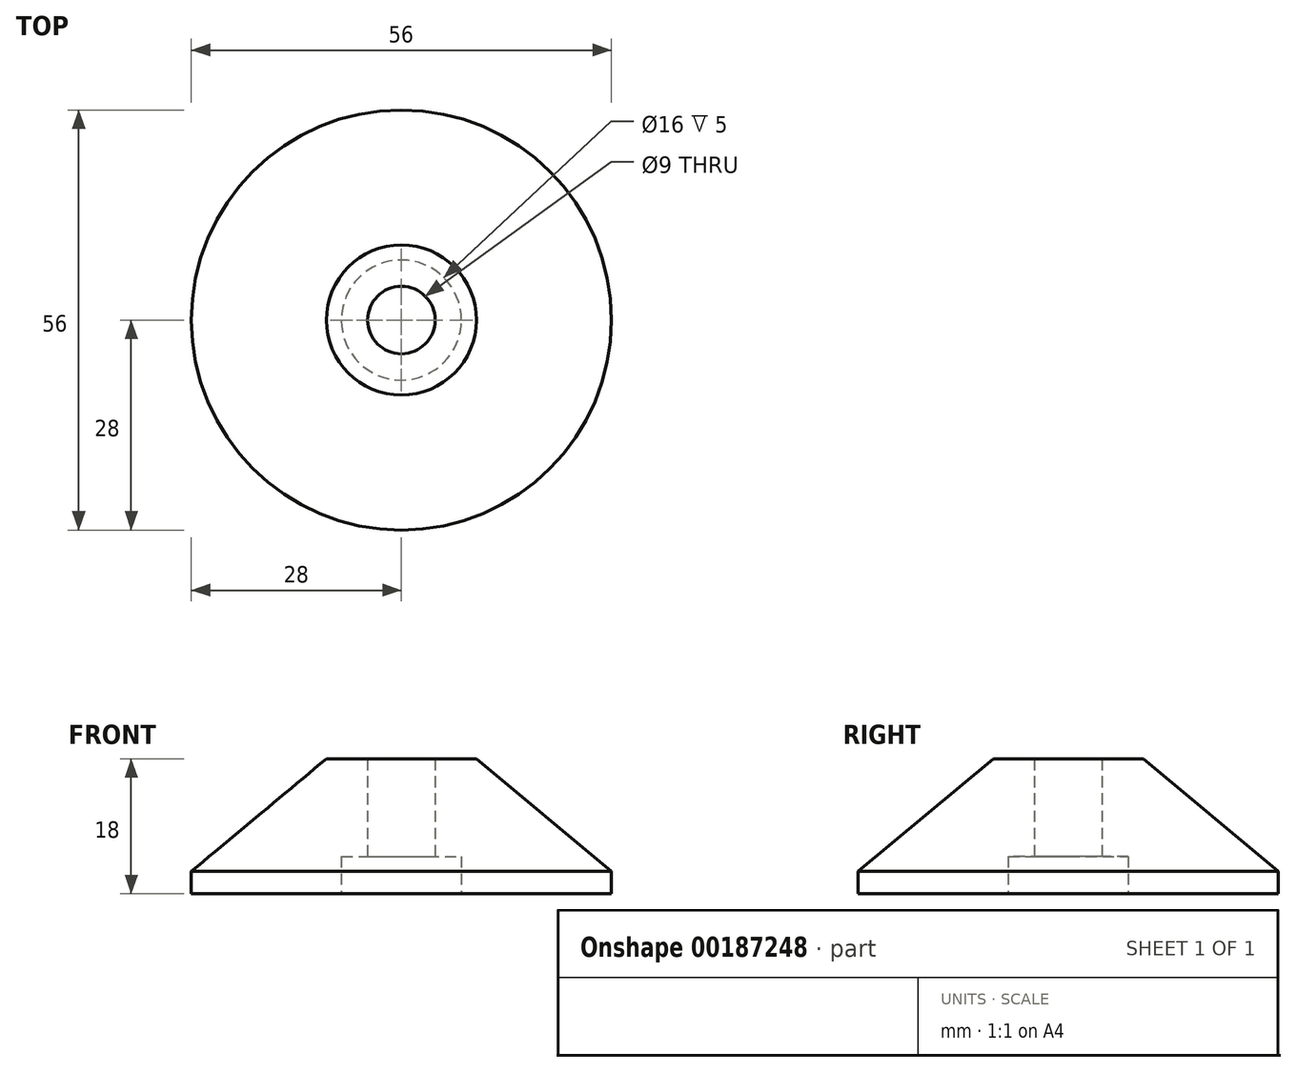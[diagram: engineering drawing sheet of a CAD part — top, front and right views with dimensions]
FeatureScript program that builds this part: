
annotation { "Feature Type Name" : "Feature", "Feature Type Description" : "" }
export const myFeature = defineFeature(function(context is Context, id is Id, definition is map)
    precondition{}
    {
        {
            var Q0;
            Q0=qCreatedBy(makeId("Front.planeOp"),FACE);
            var sketch = newSketch(context, id + "F0", { "sketchPlane" : qUnion([Q0])});
            skLineSegment(sketch, "E0", {"start": v(8, 0) * mm, "end": v(28, 0) * mm});
            skLineSegment(sketch, "E1", {"start": v(4.5, 5) * mm, "end": v(8, 5) * mm});
            skLineSegment(sketch, "E2", {"start": v(8, 5) * mm, "end": v(8, 0) * mm});
            skLineSegment(sketch, "E3", {"start": v(4.5, 18) * mm, "end": v(4.5, 5) * mm});
            skLineSegment(sketch, "E4", {"start": v(0, 0) * mm, "end": v(0, 18) * mm, "construction": true});
            skLineSegment(sketch, "E5", {"start": v(4.5, 18) * mm, "end": v(10, 18) * mm});
            skPoint(sketch, "E6.start.orphan", {"position": v(0, 35.08) * mm});
            skLineSegment(sketch, "E7", {"start": v(28, 0) * mm, "end": v(28, 3) * mm});
            skLineSegment(sketch, "E8", {"start": v(10, 18) * mm, "end": v(28, 3) * mm});
            skSolve(sketch);
        }
        {
            var Q0;
            Q0=makeQuery(id+"F0.imprint","IMPRINT",FACE,{"disambiguationData":[TD([[makeQuery(id+"F0.imprint","IMPRINT",EDGE,{"derivedFrom":sQuery(id+"F0.wireOp",EDGE,"E0")}),1.0]])]});
            var Q1;
            Q1=sQuery(id+"F0.wireOp",EDGE,"E4");
            revolve(context, id + "F1", {"entities" : qUnion([Q0]), "axis" : qUnion([Q1]), "revolveType" : RevolveType.FULL});
        }
    });
